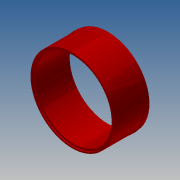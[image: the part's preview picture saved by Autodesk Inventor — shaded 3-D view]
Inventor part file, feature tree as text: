
AUTODESK INVENTOR PART (.ipt)
format: ipt  version: 2017.3 (Build 213257000, 257)  size: 152,576 bytes
history: native  units: in
note: dims shown in document units (in); Inventor stores cm internally (conversion verified against a paired STEP export)
features: extrude x4, sketch x4, chamfer x2, fillet x1
ambient origin geometry x8: Origin, YZ Plane, XZ Plane, XY Plane, X Axis, Y Axis, Z Axis, Center Point
bodies: Solid1 (feature_tree)
feature tree (11):
  extrude  "Extrusion1"  Depth=31.0in
  extrude  "Extrusion2"  Depth=12.8346in
  extrude  "Extrusion3"  Depth=1.0in
  chamfer  "Chamfer1"  Distance=1.0in
  extrude  "Extrusion4"  Depth=0.0312in TaperAngle=45.0deg
  fillet  "Fillet1"  Radius=30.0in
  chamfer  "Chamfer2"  Distance=0.5in
  sketch  "Sketch1"  dims[d0=28.5in d1=31.0in]
  sketch  "Sketch2"  dims[d2=12.8346in d3=0.0in d4=31.25in]
  sketch  "Sketch3"  dims[d5=2.0in d6=0.0in d7=30.98in d8=1.0in d9=0.0in]
  sketch  "Sketch4"  dims[d10=0.125in d11=0.125in d12=45.0deg d13=30.0in d14=0.5in d15=0.0in d16=0.0312in d17=0.0312in d18=0.125in d19=45.0deg]
